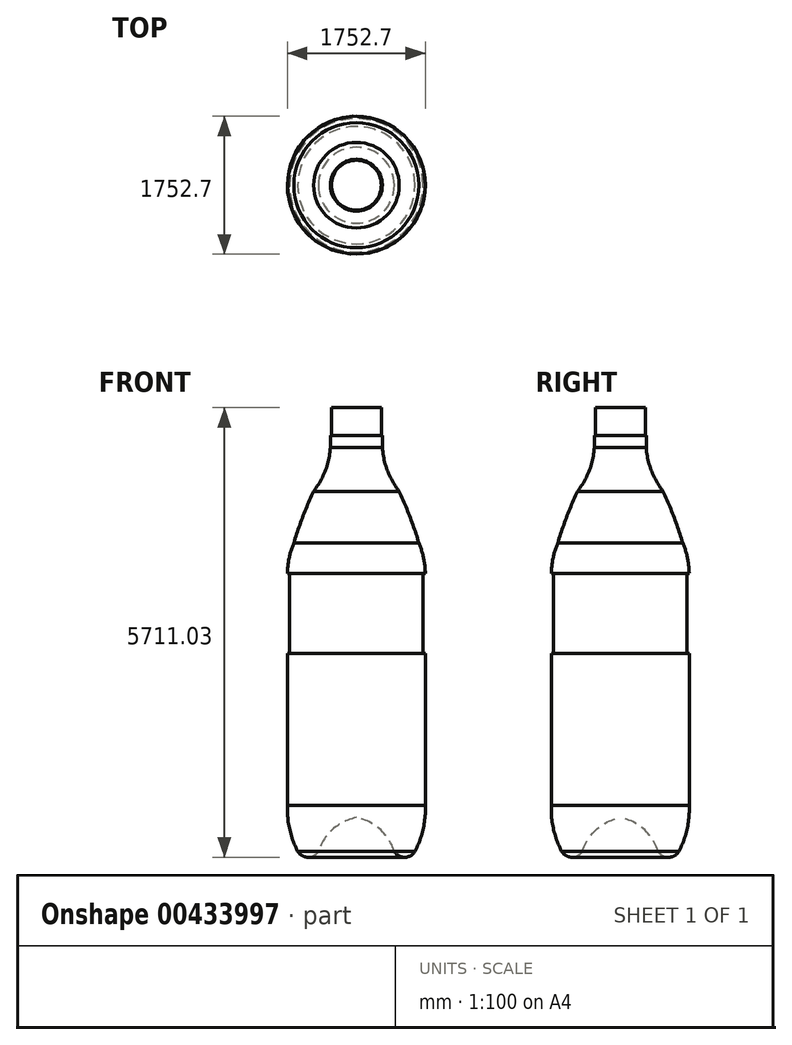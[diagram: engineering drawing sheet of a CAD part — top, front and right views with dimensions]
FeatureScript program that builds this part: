
annotation { "Feature Type Name" : "Feature", "Feature Type Description" : "" }
export const myFeature = defineFeature(function(context is Context, id is Id, definition is map)
    precondition{}
    {
        {
            var Q0;
            Q0=qCreatedBy(makeId("Front.planeOp"),FACE);
            var sketch = newSketch(context, id + "F0", { "sketchPlane" : qUnion([Q0])});
            skLineSegment(sketch, "E0", {"start": v(0, 0) * mm, "end": v(0, -1932.43) * mm});
            skLineSegment(sketch, "E1", {"start": v(0, 0) * mm, "end": v(27.94, 0) * mm});
            skLineSegment(sketch, "E2", {"start": v(27.94, 0) * mm, "end": v(27.94, 1016) * mm});
            skLineSegment(sketch, "E3", {"start": v(27.94, 1016) * mm, "end": v(0, 1016) * mm});
            skArc(sketch, "E4", {"start": v(80.56, 1400.68) * mm, "mid": v(21.5, 1212.28) * mm, "end": v(0, 1016) * mm});
            skArc(sketch, "E5", {"start": v(331.91, 2059.59) * mm, "mid": v(194.79, 1734.5) * mm, "end": v(80.56, 1400.68) * mm});
            skArc(sketch, "E6", {"start": v(0, -1932.43) * mm, "mid": v(26.52, -2231.4) * mm, "end": v(129.96, -2513.17) * mm});
            skArc(sketch, "E7", {"start": v(129.96, -2513.17) * mm, "mid": v(260.6, -2590.23) * mm, "end": v(393.06, -2516.36) * mm});
            skArc(sketch, "E8", {"start": v(875.28, -2086.21) * mm, "mid": v(575.37, -2235.36) * mm, "end": v(393.06, -2516.36) * mm});
            skArc(sketch, "E9", {"start": v(331.91, 2059.59) * mm, "mid": v(479.74, 2320.3) * mm, "end": v(545.08, 2612.79) * mm});
            skLineSegment(sketch, "E10", {"start": v(545.08, 2612.79) * mm, "end": v(545.08, 2765.19) * mm});
            skLineSegment(sketch, "E11", {"start": v(545.08, 2765.19) * mm, "end": v(557.78, 2765.19) * mm});
            skLineSegment(sketch, "E12", {"start": v(557.78, 2765.19) * mm, "end": v(557.78, 3120.79) * mm});
            skLineSegment(sketch, "E13", {"start": v(557.78, 3120.79) * mm, "end": v(875.28, 3120.79) * mm});
            skLineSegment(sketch, "E14", {"start": v(875.28, 3120.79) * mm, "end": v(875.28, -2086.21) * mm});
            skSolve(sketch);
        }
        {
            var Q0;
            Q0=makeQuery(id+"F0.imprint","IMPRINT",FACE,{"disambiguationData":[TD([[makeQuery(id+"F0.imprint","IMPRINT",EDGE,{"derivedFrom":sQuery(id+"F0.wireOp",EDGE,"E0")}),1.0]])]});
            var Q1;
            Q1=sQuery(id+"F0.wireOp",EDGE,"E14");
            revolve(context, id + "F1", {"entities" : qUnion([Q0]), "axis" : qUnion([Q1]), "revolveType" : RevolveType.FULL});
        }
    });
